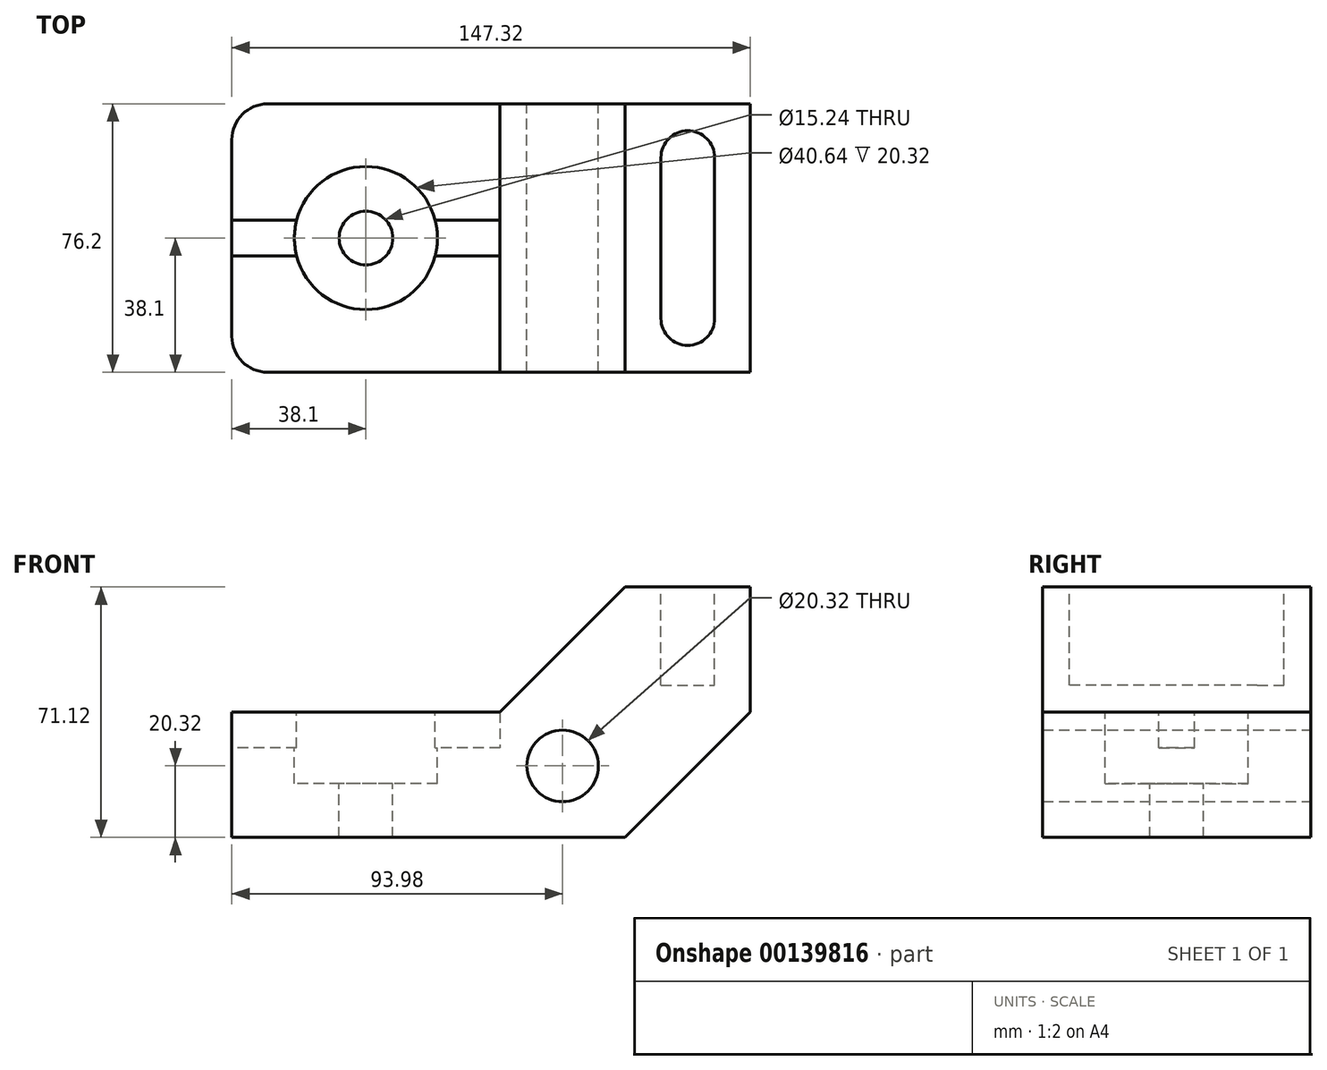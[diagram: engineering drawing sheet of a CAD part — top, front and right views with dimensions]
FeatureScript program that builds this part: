
annotation { "Feature Type Name" : "Feature", "Feature Type Description" : "" }
export const myFeature = defineFeature(function(context is Context, id is Id, definition is map)
    precondition{}
    {
        {
            var Q0;
            Q0=qCreatedBy(makeId("Front.planeOp"),FACE);
            var sketch = newSketch(context, id + "F0", { "sketchPlane" : qUnion([Q0])});
            skLineSegment(sketch, "E0", {"start": v(-111.76, 0) * mm, "end": v(0, 0) * mm});
            skLineSegment(sketch, "E1", {"start": v(0, 0) * mm, "end": v(35.56, 35.56) * mm});
            skLineSegment(sketch, "E2", {"start": v(35.56, 35.56) * mm, "end": v(35.56, 71.12) * mm});
            skLineSegment(sketch, "E3", {"start": v(35.56, 71.12) * mm, "end": v(0, 71.12) * mm});
            skLineSegment(sketch, "E4", {"start": v(0, 71.12) * mm, "end": v(-35.56, 35.56) * mm});
            skLineSegment(sketch, "E5", {"start": v(-35.56, 35.56) * mm, "end": v(-111.76, 35.56) * mm});
            skLineSegment(sketch, "E6", {"start": v(-111.76, 35.56) * mm, "end": v(-111.76, 0) * mm});
            skCircle(sketch, "E7", {"center": v(-17.78, 20.32) * mm, "radius": 10.16 * mm});
            skSolve(sketch);
        }
        {
            var Q0;
            Q0 = qSketchRegion(id + "F0", true);
            extrude(context, id + "F1", {"entities" : qUnion([Q0]), "depth" : 76.2 * mm});
        }
        {
            var Q0;
            Q0=makeQuery(id+"F1.opExtrude","CAP_EDGE",EDGE,{"disambiguationData":[OSD([sQuery(id+"F0.wireOp",EDGE,"E6")])],"isStart":false});
            var Q1;
            Q1=makeQuery(id+"F1.opExtrude","CAP_EDGE",EDGE,{"disambiguationData":[OSD([sQuery(id+"F0.wireOp",EDGE,"E6")])],"isStart":true});
            fillet(context, id + "F2", {"entities" : qUnion([Q0, Q1]), "radius" : 10.16 * mm, "tangentPropagation" : true, "allowEdgeOverflow" : false});
        }
        {
            var Q0;
            Q0=makeQuery(id+"F1.opExtrude","SWEPT_FACE",FACE,{"disambiguationData":[OSD([sQuery(id+"F0.wireOp",EDGE,"E6")])]});
            var sketch = newSketch(context, id + "F3", { "sketchPlane" : qUnion([Q0])});
            skLineSegment(sketch, "E8", {"start": v(33.02, 35.56) * mm, "end": v(33.02, 25.4) * mm});
            skLineSegment(sketch, "E9", {"start": v(33.02, 25.4) * mm, "end": v(43.18, 25.4) * mm});
            skLineSegment(sketch, "E10", {"start": v(43.18, 25.4) * mm, "end": v(43.18, 35.56) * mm});
            skLineSegment(sketch, "E11", {"start": v(43.18, 35.56) * mm, "end": v(33.02, 35.56) * mm});
            skSolve(sketch);
        }
        {
            var Q0;
            Q0=makeQuery(id+"F1.opExtrude","SWEPT_FACE",FACE,{"disambiguationData":[OSD([sQuery(id+"F0.wireOp",EDGE,"E5")])]});
            var sketch = newSketch(context, id + "F4", { "sketchPlane" : qUnion([Q0])});
            skCircle(sketch, "E12", {"center": v(-73.66, -38.1) * mm, "radius": 7.62 * mm});
            skSolve(sketch);
        }
        {
            var Q0;
            Q0=makeQuery(id+"F3.imprint","IMPRINT",FACE,{"disambiguationData":[TD([[makeQuery(id+"F3.imprint","IMPRINT",EDGE,{"derivedFrom":sQuery(id+"F3.wireOp",EDGE,"E8")}),1.0]])]});
            var Q1;
            Q1=makeQuery(id+"F1.opExtrude","SWEPT_FACE",FACE,{"disambiguationData":[OSD([sQuery(id+"F0.wireOp",EDGE,"E4")])]});
            extrude(context, id + "F5", {"entities" : qUnion([Q0]), "operationType" : NewBodyOperationType.REMOVE, "oppositeDirection" : true, "endBoundEntityFace" : qUnion([Q1]), "depth" : 76.2 * mm});
        }
        {
            var Q0;
            Q0=makeQuery(id+"F1.opExtrude","SWEPT_FACE",FACE,{"disambiguationData":[OSD([sQuery(id+"F0.wireOp",EDGE,"E3")])]});
            var sketch = newSketch(context, id + "F6", { "sketchPlane" : qUnion([Q0])});
            skLineSegment(sketch, "E13", {"start": v(25.4, -60.96) * mm, "end": v(25.4, -15.24) * mm});
            skLineSegment(sketch, "E14", {"start": v(10.16, -15.24) * mm, "end": v(10.16, -60.96) * mm});
            skArc(sketch, "E15", {"start": v(10.16, -60.96) * mm, "mid": v(17.78, -68.58) * mm, "end": v(25.4, -60.96) * mm});
            skArc(sketch, "E16", {"start": v(25.4, -15.24) * mm, "mid": v(17.78, -7.62) * mm, "end": v(10.16, -15.24) * mm});
            skSolve(sketch);
        }
        {
            var Q0;
            Q0=makeQuery(id+"F6.imprint","IMPRINT",FACE,{"disambiguationData":[TD([[makeQuery(id+"F6.imprint","IMPRINT",EDGE,{"derivedFrom":sQuery(id+"F6.wireOp",EDGE,"E13")}),1.0]])]});
            extrude(context, id + "F7", {"entities" : qUnion([Q0]), "operationType" : NewBodyOperationType.REMOVE, "oppositeDirection" : true, "depth" : 27.94 * mm});
        }
        {
            var Q0;
            Q0=sQuery(id+"F4.wireOp",VERTEX,"E12.center");
            var Q1;
            Q1=makeQuery(id+"F1.opExtrude","SWEPT_BODY",BODY,{"disambiguationData":[OSD([sQuery(id+"F0.wireOp",EDGE,"E0"),sQuery(id+"F0.wireOp",EDGE,"E1"),sQuery(id+"F0.wireOp",EDGE,"E2"),sQuery(id+"F0.wireOp",EDGE,"E3"),sQuery(id+"F0.wireOp",EDGE,"E4"),sQuery(id+"F0.wireOp",EDGE,"E5"),sQuery(id+"F0.wireOp",EDGE,"E6"),sQuery(id+"F0.wireOp",EDGE,"E7")])]});
            hole(context, id + "F8", {"style" : HoleStyle.C_BORE, "endStyle" : HoleEndStyle.THROUGH, "holeDiameter" : 15.24 * mm, "cBoreDiameter" : 40.64 * mm, "cBoreDepth" : 10.16 * mm, "locations" : qUnion([Q0]), "scope" : qUnion([Q1]), "isTappedThrough" : true});
        }
    });
